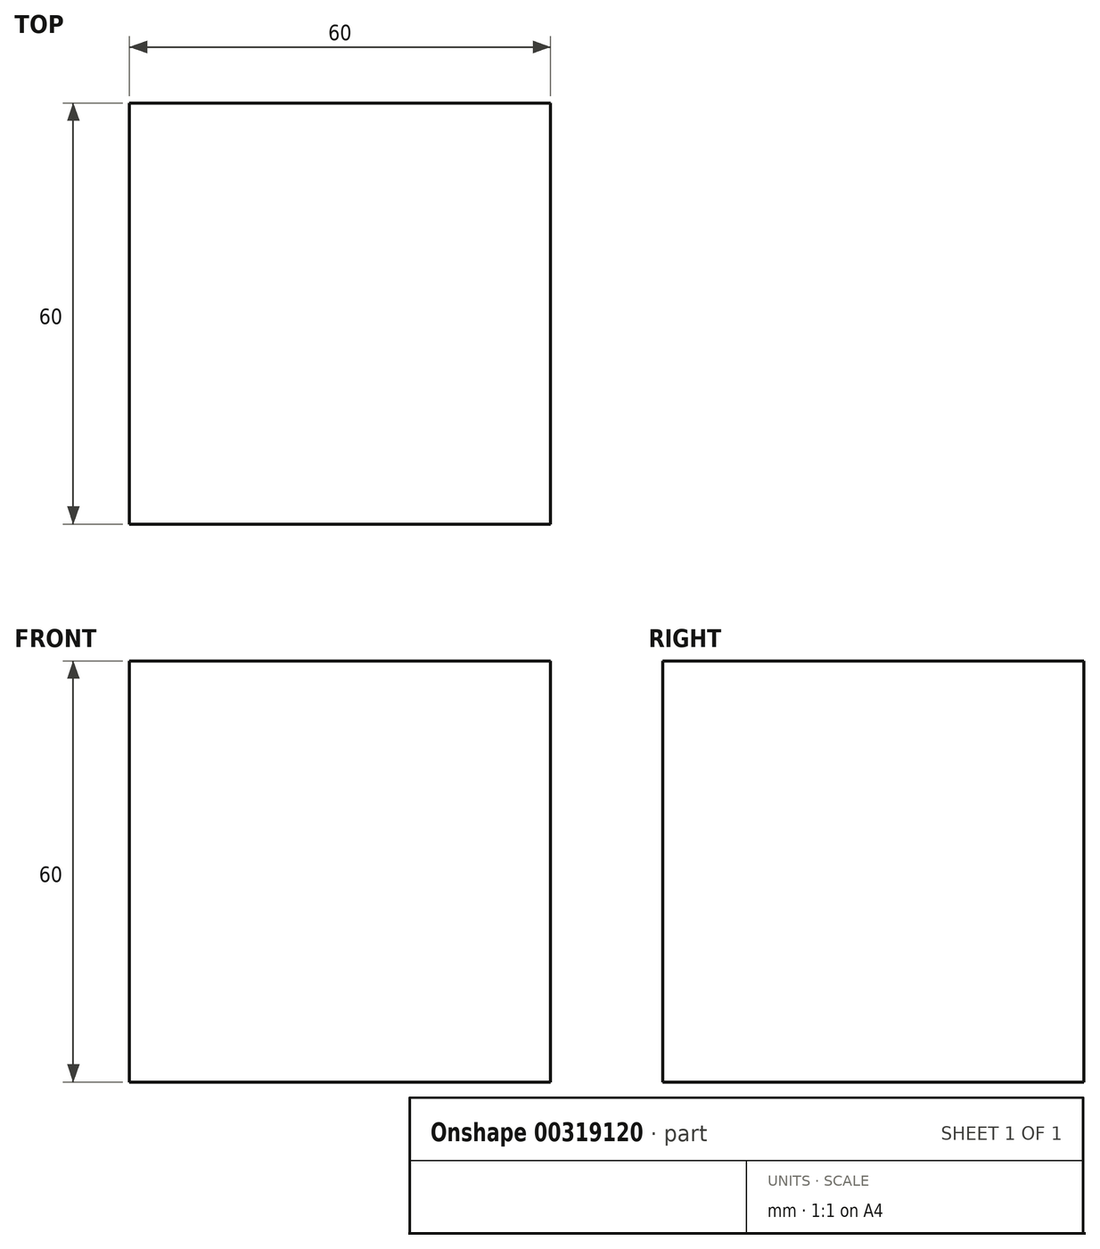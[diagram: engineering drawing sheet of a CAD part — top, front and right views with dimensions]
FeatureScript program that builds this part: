
annotation { "Feature Type Name" : "Feature", "Feature Type Description" : "" }
export const myFeature = defineFeature(function(context is Context, id is Id, definition is map)
    precondition{}
    {
        {
            var Q0;
            Q0=qCreatedBy(makeId("Front.planeOp"),FACE);
            var sketch = newSketch(context, id + "F0", { "sketchPlane" : qUnion([Q0])});
            skLineSegment(sketch, "E0.bottom", {"start": v(0, 0) * mm, "end": v(60, 0) * mm});
            skLineSegment(sketch, "E0.top", {"start": v(0, 60) * mm, "end": v(60, 60) * mm});
            skLineSegment(sketch, "E0.left", {"start": v(0, 0) * mm, "end": v(0, 60) * mm});
            skLineSegment(sketch, "E0.right", {"start": v(60, 0) * mm, "end": v(60, 60) * mm});
            skSolve(sketch);
        }
        {
            var Q0;
            Q0 = qSketchRegion(id + "F0", true);
            extrude(context, id + "F1", {"entities" : qUnion([Q0]), "depth" : 60 * mm});
        }
    });
